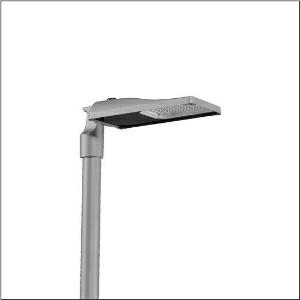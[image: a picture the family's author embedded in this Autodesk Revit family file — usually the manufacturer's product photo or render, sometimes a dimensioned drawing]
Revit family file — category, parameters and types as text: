
# Revit family: streetlight_sl_31_mini___st1_0a_5xh6d3as08ga_7bf7
name_source: partatom
category: Lighting Fixtures
units: mm (PartAtom-declared; Revit-internal decimal feet)

## family parameters
Cut with Voids When Loaded = No
Host = Face
Light Source = No
Part Type = Normal
Room Calculation Point = No
Round Connector Dimension = Use Diameter
Shared = No

## types (1)
- --- (1 x LED, 5880 lm, 39.3 W, 3000K)
    Apparent Load = 39 VA
    CIE Flux Codes = 37 72 97 100 100
    Color Rendering = 70
    Color Temperature = 3000K
    Default Elevation = 1800 mm
    Description = Streetlight SL 31 mini D4i mast luminaire for post-top, side-entry; light control with lens of PMMA; light distribution: ST1.0a, direct asymmetric distribution, for standard-compliant lighting for roads and squares; LED: luminous flux: 5.880lm, light colour: 730, colour temperature: 3000K; luminous efficacy: 149,6lm/W; control: pre-setting: logarithmic dimming characteristic, flexible luminous flux parameterisation, time-dependent luminous flux control, constant luminous flux control, power reduction, intelligent temperature release in ECG and LED module, overheat protection; luminaire housing, of diecast aluminium, Siteco® metallic grey (DB 702S), corrosivity category C5 high according to DIN EN ISO 12944; cover of toughened safety glass, transparent, opened without tools; mast flange of diecast aluminium, Siteco® metallic grey (DB 702S), spigot size: 76/60mm, mast flange included unmounted; with cable H07RN-F 2x 1.5mm², cable length: 6,5m, connection cable pre-assembled; mains connection: 220..240V, AC, 50/60Hz; power consumption (at start of service life): 39,3W / (at end of service life): 40,7W / (with reduced operation 50%): 18,1W; protection rating (complete): IP66; insulation class (complete): insulation class II (safety insulation); impact resistance: IK10; certification: CE, ENEC, ENEC+, VDE, UKCA, ZD4i; permissible operating ambient temperature for outdoor applications: -40..+50°C; packaging unit: 1 piece

Light Distribution: ST1.0a
    Height = 76 mm
    Lamp = 1 x LED
    Lamp Light Flux = 5880 lm
    Lamp Power = 39.3 W
    Lamp count = 1
    Length = 547 mm
    Luminous efficacy = 150 lm/W
    Manufacturer = Siteco
    ModVariant = No
    Model = 5XH6D3AS08GA
    Number of Poles = 1
    OnlyDefault = Yes
    Power Factor = 1
    Product Name = Streetlight SL 31 mini | ST1.0a
    Product group = mast luminaire | pylon top
    ProductGroupID = 6100
    Protection Class = Protection class II
    Protection Degree = IP 66
    RLX_Detail_Level = 1
    RLX_Emergency_Light_Flux = 0 lm
    RLX_Emergency_Type = 0
    RLX_Emergency_Type_DB = No
    RlxData = <blob elided: 39577 chars, md5=39966144>
    Socket = socket
    Standby Power = 0 W
    System Light Flux = 5880 lm
    System Power = 39 W
    Type Comments = factory setting: luminous flux: 100 % | dim-lin: 254 | 798 mA
    Type Image = l_1300330.jpg
    URL = http://relux.com
    VarID = @adj_074347
    Voltage = 0 V
    Weight = 0.00 kg
    Width = 265 mm

## geometry (parser evidence)
native form markers: Blend x4, Sweep x9
no freeform markers — native parametric forms only
